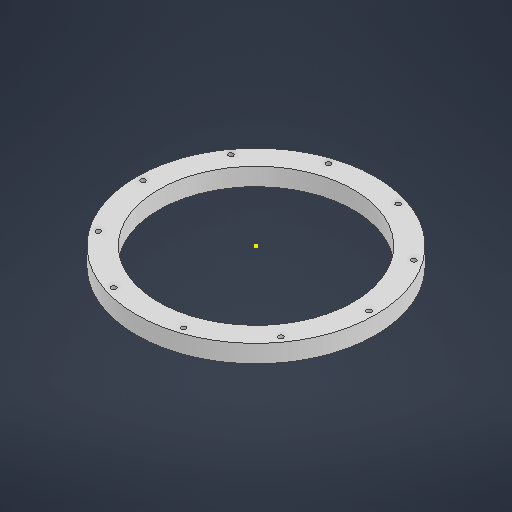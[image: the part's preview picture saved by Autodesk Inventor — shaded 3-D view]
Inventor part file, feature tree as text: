
AUTODESK INVENTOR PART (.ipt)
format: ipt  version: 2025 (Build 290162000, 162)  size: 220,672 bytes
history: native  units: in
note: dims shown in document units (in); Inventor stores cm internally (conversion verified against a paired STEP export)
features: sketch x4, extrude x1, hole x1
ambient origin geometry x8: Origin, YZ Plane, XZ Plane, XY Plane, X Axis, Y Axis, Z Axis, Center Point
bodies: Solid1 (feature_tree)
feature tree (6):
  extrude  "Extrusion1"  Depth=8.6614in
  hole  "Hole1"  [1 undecoded]
  sketch  "Sketch7"  dims[d10=3.937in d12=360.0deg d14=0.2165in d15=0.3937in d16=0.1575in d17=0.0787in d18=90.0deg d19=0.315in d20=0.8108in d24=0.0197in d25=0.0344in d26=0.0197in d27=0.0344in d30=0.0197in d31=0.0344in d32=0.0197in d33=0.0344in]
  sketch  "Sketch1"  dims[d0=10.6299in d1=8.6614in]
  sketch  "Sketch3"  dims[d9=0.1575in]
  sketch  "Sketch Circular Pattern1"  dims[d2=0.7874in d3=0.0in d8=10.0394in]
note: 1 required parameter value undecoded (feature->parameter linkage not recoverable at this tier; creation-order binding heuristic only, values carry confidence <= 0.55)
